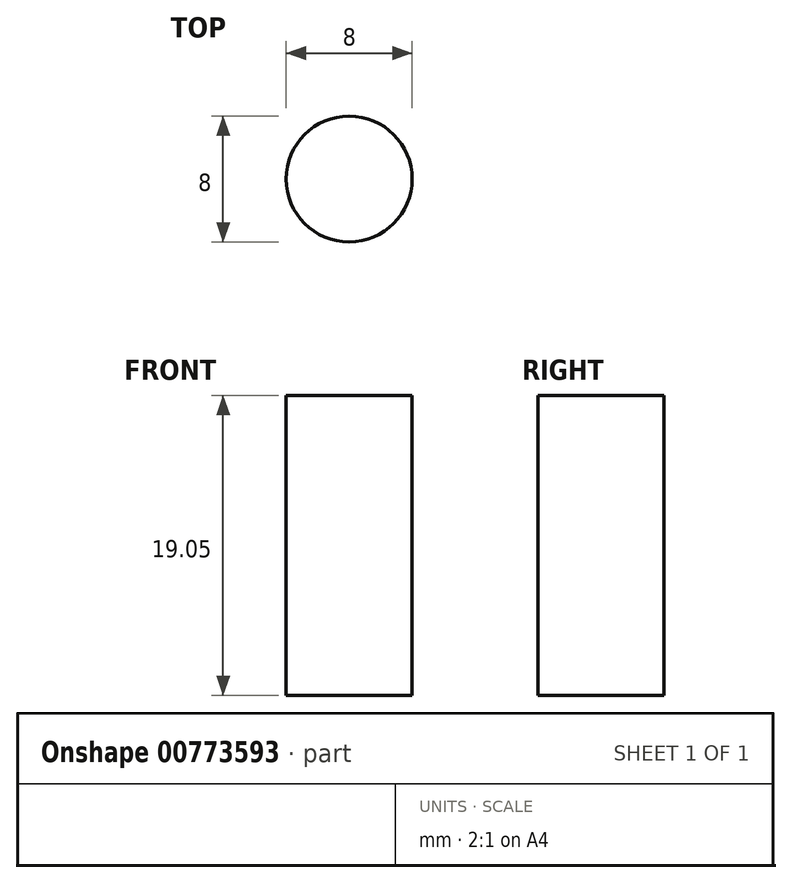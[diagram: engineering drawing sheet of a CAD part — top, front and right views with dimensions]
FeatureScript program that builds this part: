
annotation { "Feature Type Name" : "Feature", "Feature Type Description" : "" }
export const myFeature = defineFeature(function(context is Context, id is Id, definition is map)
    precondition{}
    {
        {
            var Q0;
            Q0=qCreatedBy(makeId("Top.planeOp"),FACE);
            var sketch = newSketch(context, id + "F0", { "sketchPlane" : qUnion([Q0])});
            skCircle(sketch, "E0", {"center": v(0, 0) * mm, "radius": 4 * mm});
            skSolve(sketch);
        }
        {
            var Q0;
            Q0 = qSketchRegion(id + "F0", true);
            extrude(context, id + "F1", {"entities" : qUnion([Q0]), "depth" : 19.05 * mm, "offsetDistance" : 25.4 * mm});
        }
    });
